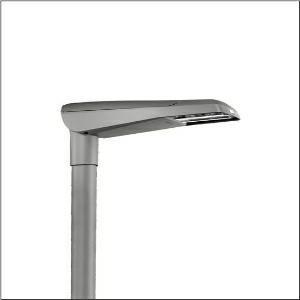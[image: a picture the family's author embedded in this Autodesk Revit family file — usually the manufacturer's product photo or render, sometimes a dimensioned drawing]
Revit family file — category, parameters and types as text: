
# Revit family: streetlight_sl_11_iq_micro___st1_2a_5xc1ac1g08ce_7479
name_source: partatom
category: Lighting Fixtures
units: mm (PartAtom-declared; Revit-internal decimal feet)

## family parameters
Cut with Voids When Loaded = No
Host = Face
Light Source = No
Part Type = Normal
Room Calculation Point = No
Round Connector Dimension = Use Diameter
Shared = No

## types (1)
- --- (1 x LED, 1600 lm, 14 W, 2200K)
    Apparent Load = 14 VA
    CIE Flux Codes = 33 71 96 100 100
    Color Rendering = 70
    Color Temperature = 2200K
    Default Elevation = 1800 mm
    Description = Streetlight SL 11 iQ micro, mast luminaire, primary light control with 3 zone facetted reflector, of plastic, silver coated, highly specular, primary optical cover: cover, of PMMA, transparent, light distribution: ST1.2a, light emission: direct distribution, primary light characteristic: asymmetric, installation type: post-top, side-entry, lamps: LED, High Power LED, rated values: 1.880lm | 13,8W | 136,2lm/W (begin service life); end service life: 1.880lm | 14W; at 50% lumin. flux: 940lm | 7,5W | 125,3lm/W, colour temperature: 2200/2700/3000/4000K, colour rendering: CRI > 70, light colour: 722/727/730/740, light setting 1 begin service life: 100% | 1.880lm | 13,8W | 136,2lm/W | 3.000K, light setting 1 end service life: 14W, further light settings possible, control: pre-setting: linear dimming characteristic, Street-Remote, Auto-Match, Temp-Guard, Lumen-Switch, Night-Set, Smart-Wire, Light-Fading, Desk-Remote (wireless, voltage-free reading and setting of iQ features in the workshop via application-optimized NFC function/RFID function), optimised constant luminous flux control (CLO 2.0), with cable H07RN-F 5x 1.5mm², mains connection: 220..240V, AC, 50/60Hz, connection cable pre-assembled, cable length: 5,5m, luminaire housing, of diecast aluminium, powder-coated, Siteco® metallic grey (DB 702S), please order mast flange separately, inclination adjustable without tools: 0°, 5°, 10°, 15° (post-top) | 0°, -5°, -10°, -15° (side-entry), sealing non-destructively replaceable, multi-level sealing system, length: 600mm, width: 174mm, height: 116mm, mast flange for spigot size: 42mm (side-entry): 5XC10008XM4, 60/48mm (side-entry/post-top): 5XC10108XM2, 76/60mm (side-entry/post-top): 5XC10108XM1, equipment: standard, protection rating (complete): IP66, insulation class (complete): insulation class II (safety insulation), certification: CE, ENEC, ENEC+, VDE, impact resistance: IK10, permissible operating ambient temperature for outdoor applications: -25..+50°C, standard-compliant lighting for roads and squares, Environmental Product Declaration (EPD) tested and certified by an independent institute, packaging unit: 1 piece

Light Distribution: ST1.2a
    Height = 116 mm
    Lamp = 1 x LED
    Lamp Light Flux = 1600 lm
    Lamp Power = 14 W
    Lamp count = 1
    Length = 600 mm
    Luminous efficacy = 114 lm/W
    Manufacturer = Siteco
    ModVariant = No
    Model = 5XC1AC1G08CE
    Number of Poles = 1
    OnlyDefault = Yes
    Power Factor = 1
    Product Name = Streetlight SL 11 iQ micro | ST1.2a
    Product group = mast luminaire | pylon top
    ProductGroupID = 6100
    Protection Class = Protection class II
    Protection Degree = IP 66
    RLX_Detail_Level = 1
    RLX_Emergency_Light_Flux = 0 lm
    RLX_Emergency_Type = 0
    RLX_Emergency_Type_DB = No
    RlxData = <blob elided: 58597 chars, md5=ba96a059>
    Socket = socket
    Standby Power = 0 W
    System Light Flux = 1600 lm
    System Power = 14 W
    Type Comments = individual setting: luminous flux: 100 % | dim-lin: 254 | 369 mA
    Type Image = l_1006566.jpg
    URL = http://relux.com
    VarID = @adj_035188
    Voltage = 0 V
    Weight = 0.00 kg
    Width = 174 mm

## geometry (parser evidence)
native form markers: Blend x4, Sweep x12
no freeform markers — native parametric forms only
